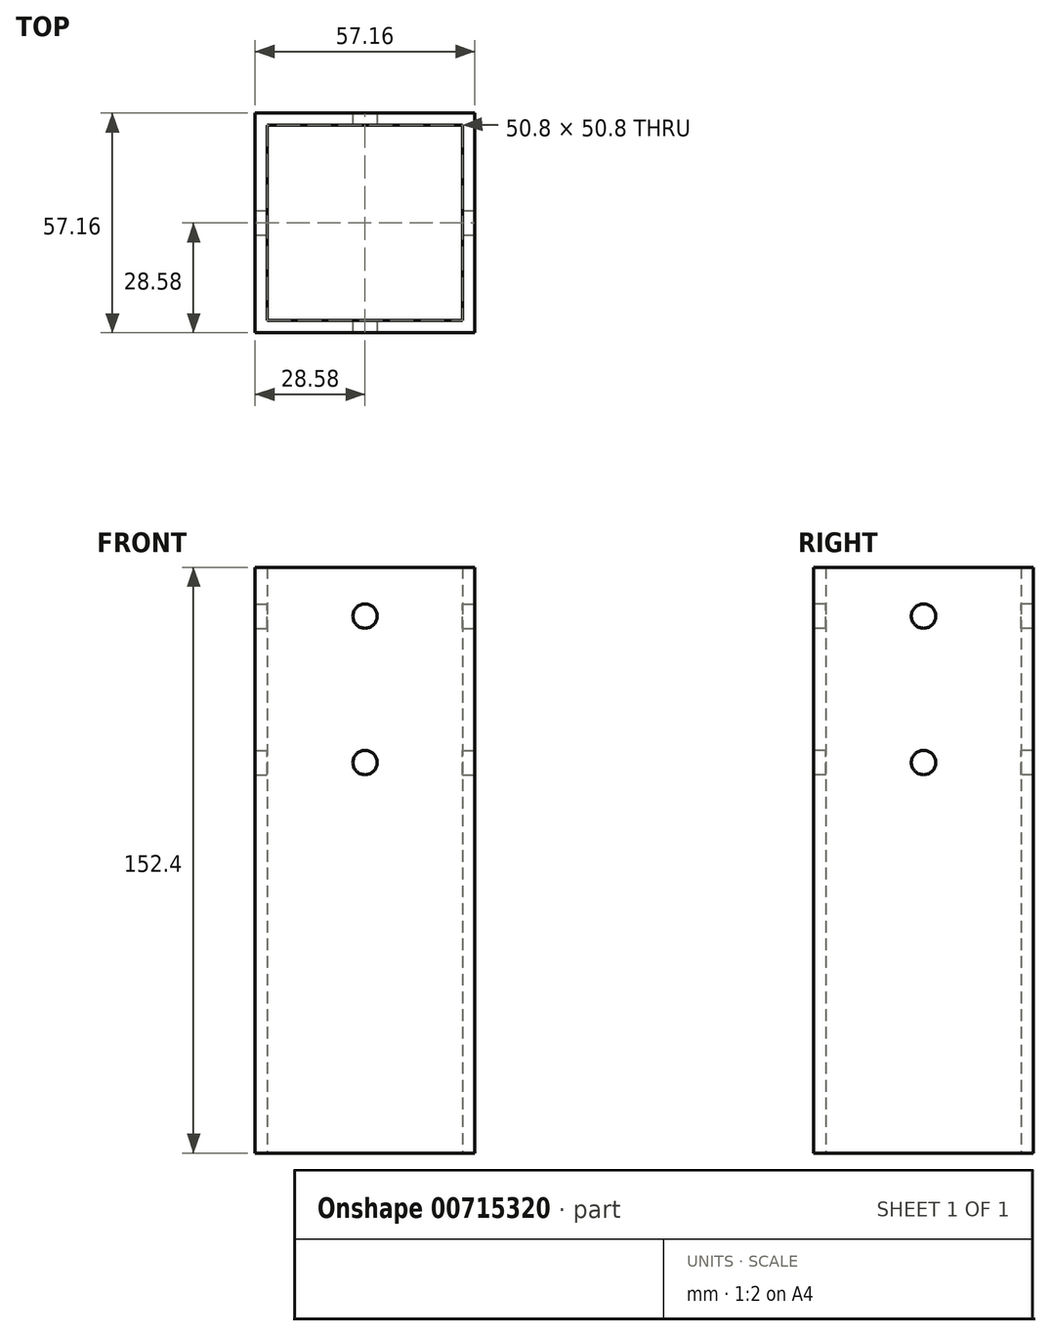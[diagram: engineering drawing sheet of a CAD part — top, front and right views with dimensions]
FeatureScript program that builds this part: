
annotation { "Feature Type Name" : "Feature", "Feature Type Description" : "" }
export const myFeature = defineFeature(function(context is Context, id is Id, definition is map)
    precondition{}
    {
        {
            var Q0;
            Q0=qCreatedBy(makeId("Top.planeOp"),FACE);
            var sketch = newSketch(context, id + "F0", { "sketchPlane" : qUnion([Q0])});
            skLineSegment(sketch, "E0.bottom", {"start": v(25.4, 25.4) * mm, "end": v(-25.4, 25.4) * mm});
            skLineSegment(sketch, "E0.top", {"start": v(25.4, -25.4) * mm, "end": v(-25.4, -25.4) * mm});
            skLineSegment(sketch, "E0.left", {"start": v(25.4, 25.4) * mm, "end": v(25.4, -25.4) * mm});
            skLineSegment(sketch, "E0.right", {"start": v(-25.4, 25.4) * mm, "end": v(-25.4, -25.4) * mm});
            skPoint(sketch, "E0.middle", {"position": v(0, 0) * mm});
            skLineSegment(sketch, "E1.0", {"start": v(-28.58, 28.58) * mm, "end": v(-28.58, -28.57) * mm});
            skLineSegment(sketch, "E1.1", {"start": v(28.58, 28.58) * mm, "end": v(-28.58, 28.58) * mm});
            skLineSegment(sketch, "E1.2", {"start": v(28.58, 28.58) * mm, "end": v(28.57, -28.58) * mm});
            skLineSegment(sketch, "E1.3", {"start": v(28.57, -28.57) * mm, "end": v(-28.58, -28.57) * mm});
            skSolve(sketch);
        }
        {
            var Q0;
            Q0 = qSketchRegion(id + "F0", true);
            extrude(context, id + "F1", {"entities" : qUnion([Q0]), "depth" : 152.4 * mm, "offsetDistance" : 25.4 * mm});
        }
        {
            var Q0;
            Q0=makeQuery(id+"F1.opExtrude","SWEPT_FACE",FACE,{"disambiguationData":[OSD([sQuery(id+"F0.wireOp",EDGE,"E1.3")])]});
            var sketch = newSketch(context, id + "F2", { "sketchPlane" : qUnion([Q0])});
            skCircle(sketch, "E2", {"center": v(0, 139.7) * mm, "radius": 3.18 * mm});
            skCircle(sketch, "E3", {"center": v(0, 101.6) * mm, "radius": 3.18 * mm});
            skSolve(sketch);
        }
        {
            var Q0;
            Q0 = qSketchRegion(id + "F2", true);
            extrude(context, id + "F3", {"entities" : qUnion([Q0]), "operationType" : NewBodyOperationType.REMOVE, "endBound" : BoundingType.THROUGH_ALL, "oppositeDirection" : true, "depth" : 25.4 * mm, "offsetDistance" : 25.4 * mm});
        }
        {
            var Q0;
            Q0=makeQuery(id+"F1.opExtrude","SWEPT_FACE",FACE,{"disambiguationData":[OSD([sQuery(id+"F0.wireOp",EDGE,"E1.2")])]});
            var sketch = newSketch(context, id + "F4", { "sketchPlane" : qUnion([Q0])});
            skCircle(sketch, "E4", {"center": v(0, 139.7) * mm, "radius": 3.17 * mm});
            skCircle(sketch, "E5", {"center": v(0, 101.6) * mm, "radius": 3.18 * mm});
            skSolve(sketch);
        }
        {
            var Q0;
            Q0 = qSketchRegion(id + "F4", true);
            extrude(context, id + "F5", {"entities" : qUnion([Q0]), "operationType" : NewBodyOperationType.REMOVE, "endBound" : BoundingType.THROUGH_ALL, "oppositeDirection" : true, "depth" : 25.4 * mm, "offsetDistance" : 25.4 * mm});
        }
    });
